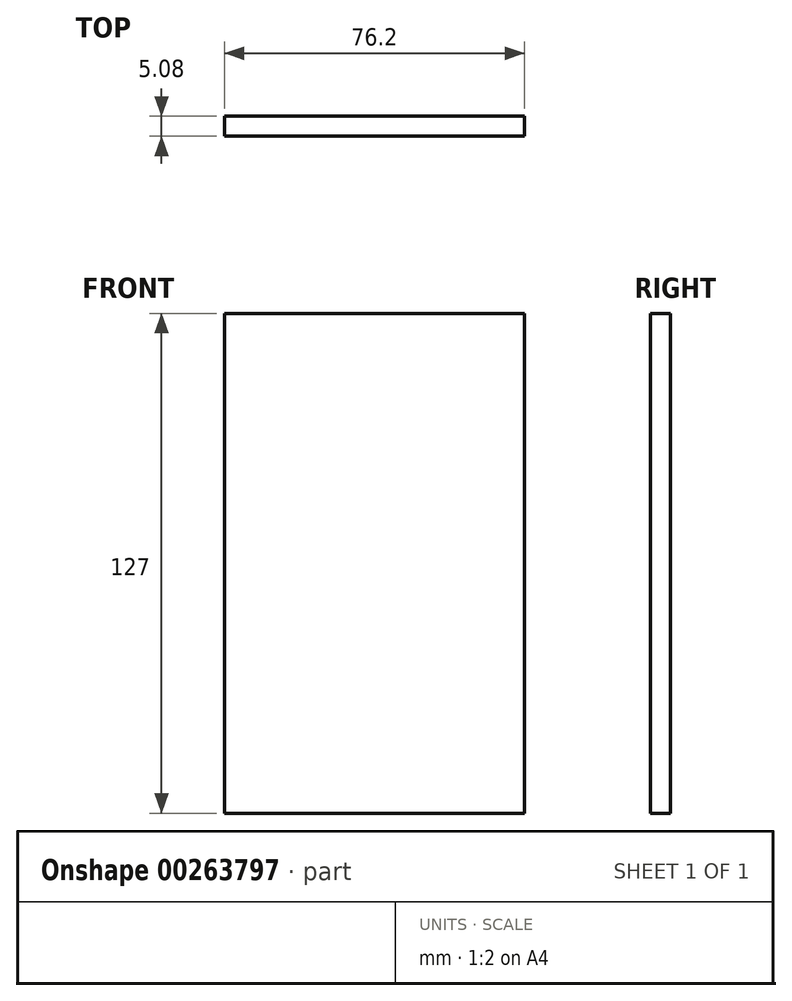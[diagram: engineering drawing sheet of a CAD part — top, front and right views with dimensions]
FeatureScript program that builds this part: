
annotation { "Feature Type Name" : "Feature", "Feature Type Description" : "" }
export const myFeature = defineFeature(function(context is Context, id is Id, definition is map)
    precondition{}
    {
        {
            var Q0;
            Q0=qCreatedBy(makeId("Front.planeOp"),FACE);
            var sketch = newSketch(context, id + "F0", { "sketchPlane" : qUnion([Q0])});
            skLineSegment(sketch, "E0.bottom", {"start": v(-38.1, 63.5) * mm, "end": v(38.1, 63.5) * mm});
            skLineSegment(sketch, "E0.top", {"start": v(-38.1, -63.5) * mm, "end": v(38.1, -63.5) * mm});
            skLineSegment(sketch, "E0.left", {"start": v(-38.1, 63.5) * mm, "end": v(-38.1, -63.5) * mm});
            skLineSegment(sketch, "E0.right", {"start": v(38.1, 63.5) * mm, "end": v(38.1, -63.5) * mm});
            skPoint(sketch, "E0.middle", {"position": v(0, 0) * mm});
            skSolve(sketch);
        }
        {
            var Q0;
            Q0 = qSketchRegion(id + "F0", true);
            extrude(context, id + "F1", {"entities" : qUnion([Q0]), "depth" : 5.08 * mm});
        }
    });
